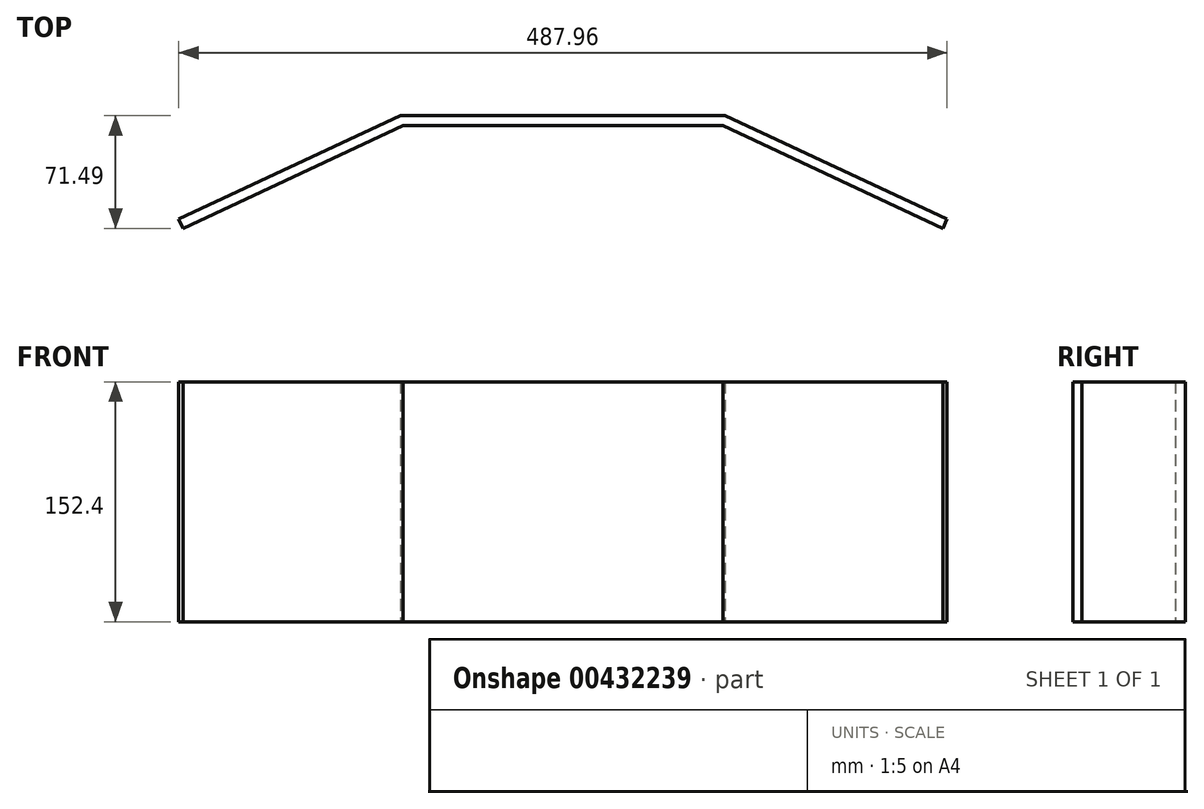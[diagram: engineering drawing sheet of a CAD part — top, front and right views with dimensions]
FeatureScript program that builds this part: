
annotation { "Feature Type Name" : "Feature", "Feature Type Description" : "" }
export const myFeature = defineFeature(function(context is Context, id is Id, definition is map)
    precondition{}
    {
        {
            var Q0;
            Q0=qCreatedBy(makeId("Top.planeOp"),FACE);
            var sketch = newSketch(context, id + "F0", { "sketchPlane" : qUnion([Q0])});
            skLineSegment(sketch, "E0", {"start": v(-157.36, 0) * mm, "end": v(45.84, 0) * mm});
            skLineSegment(sketch, "E1", {"start": v(45.84, 0) * mm, "end": v(185.54, -65.14) * mm});
            skLineSegment(sketch, "E2", {"start": v(-157.36, 0) * mm, "end": v(-297.06, -65.14) * mm});
            skLineSegment(sketch, "E3.0", {"start": v(-158.77, 6.35) * mm, "end": v(-299.74, -59.39) * mm});
            skLineSegment(sketch, "E3.1", {"start": v(-158.77, 6.35) * mm, "end": v(47.25, 6.35) * mm});
            skLineSegment(sketch, "E3.2", {"start": v(47.25, 6.35) * mm, "end": v(188.22, -59.39) * mm});
            skLineSegment(sketch, "E4", {"start": v(-299.74, -59.39) * mm, "end": v(-297.06, -65.14) * mm});
            skLineSegment(sketch, "E5", {"start": v(188.22, -59.39) * mm, "end": v(185.54, -65.14) * mm});
            skSolve(sketch);
        }
        {
            var Q0;
            Q0 = qSketchRegion(id + "F0", true);
            extrude(context, id + "F1", {"entities" : qUnion([Q0]), "depth" : 152.4 * mm});
        }
    });
